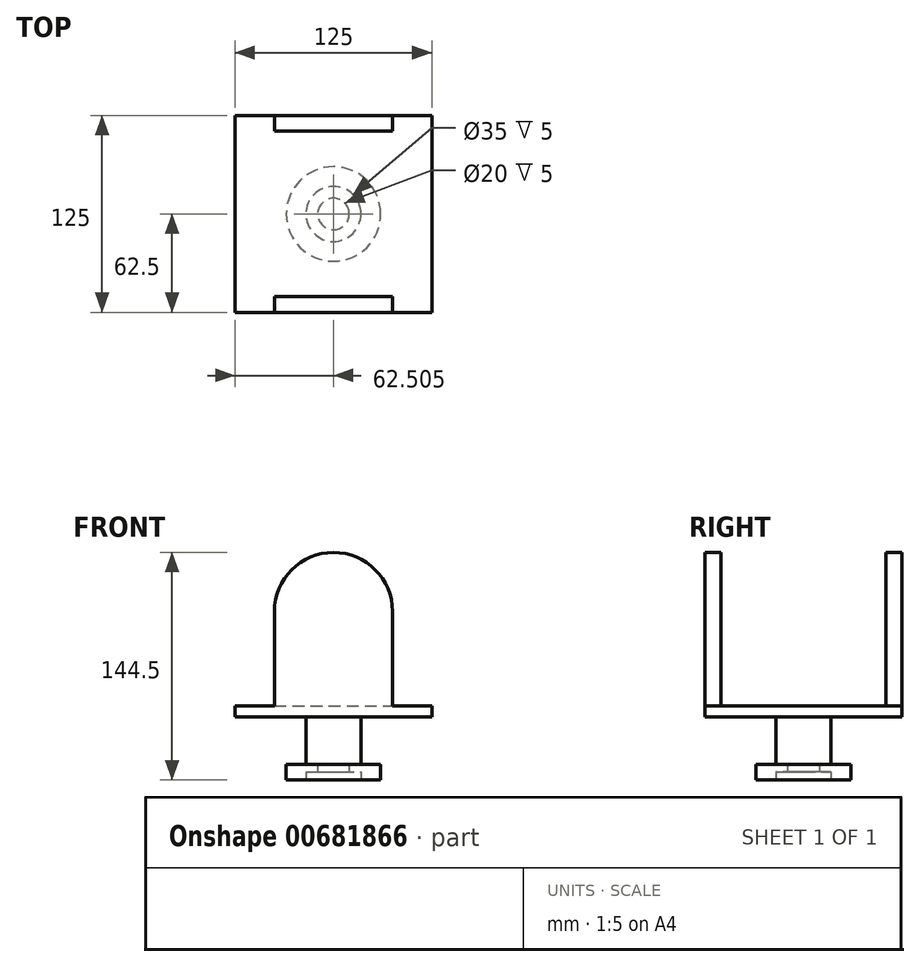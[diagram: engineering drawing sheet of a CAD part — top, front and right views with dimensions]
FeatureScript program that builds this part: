
annotation { "Feature Type Name" : "Feature", "Feature Type Description" : "" }
export const myFeature = defineFeature(function(context is Context, id is Id, definition is map)
    precondition{}
    {
        {
            var Q0;
            Q0=qCreatedBy(makeId("Front.planeOp"),FACE);
            var sketch = newSketch(context, id + "F0", { "sketchPlane" : qUnion([Q0])});
            skLineSegment(sketch, "E0.bottom", {"start": v(-61.18, -9.1) * mm, "end": v(63.82, -9.1) * mm});
            skLineSegment(sketch, "E0.top", {"start": v(-61.18, -16.1) * mm, "end": v(63.82, -16.1) * mm});
            skLineSegment(sketch, "E0.left", {"start": v(-61.18, -9.1) * mm, "end": v(-61.18, -16.1) * mm});
            skLineSegment(sketch, "E0.right", {"start": v(63.82, -9.1) * mm, "end": v(63.82, -16.1) * mm});
            skSolve(sketch);
        }
        {
            var Q0;
            Q0 = qSketchRegion(id + "F0", true);
            extrude(context, id + "F1", {"entities" : qUnion([Q0]), "depth" : 105 * mm, "offsetDistance" : 25 * mm});
        }
        {
            var Q0;
            Q0=makeQuery(id+"F1.opExtrude","CAP_FACE",FACE,{"disambiguationData":[OSD([sQuery(id+"F0.wireOp",EDGE,"E0.bottom"),sQuery(id+"F0.wireOp",EDGE,"E0.top"),sQuery(id+"F0.wireOp",EDGE,"E0.left"),sQuery(id+"F0.wireOp",EDGE,"E0.right")])],"isStart":false});
            var sketch = newSketch(context, id + "F2", { "sketchPlane" : qUnion([Q0])});
            skLineSegment(sketch, "E1.bottom", {"start": v(-61.18, -16.1) * mm, "end": v(63.82, -16.1) * mm});
            skLineSegment(sketch, "E1.top", {"start": v(-61.18, -9.1) * mm, "end": v(63.82, -9.1) * mm});
            skLineSegment(sketch, "E1.left", {"start": v(-61.18, -16.1) * mm, "end": v(-61.18, -9.1) * mm});
            skLineSegment(sketch, "E1.right", {"start": v(63.82, -16.1) * mm, "end": v(63.82, -9.1) * mm});
            skLineSegment(sketch, "E2.bottom", {"start": v(-36.18, -9.1) * mm, "end": v(38.82, -9.1) * mm});
            skLineSegment(sketch, "E2.top", {"start": v(-36.18, 50.9) * mm, "end": v(38.82, 50.9) * mm});
            skLineSegment(sketch, "E2.left", {"start": v(-36.18, -9.1) * mm, "end": v(-36.18, 50.9) * mm});
            skLineSegment(sketch, "E2.right", {"start": v(38.82, -9.1) * mm, "end": v(38.82, 50.9) * mm});
            skArc(sketch, "E3", {"start": v(38.82, 50.9) * mm, "mid": v(1.32, 88.4) * mm, "end": v(-36.18, 50.9) * mm});
            skSolve(sketch);
        }
        {
            var Q0;
            Q0 = qSketchRegion(id + "F2", true);
            extrude(context, id + "F3", {"entities" : qUnion([Q0]), "operationType" : NewBodyOperationType.ADD, "depth" : 10 * mm, "offsetDistance" : 25 * mm});
        }
        {
            var Q0;
            Q0=makeQuery(id+"F1.opExtrude","CAP_FACE",FACE,{"disambiguationData":[OSD([sQuery(id+"F0.wireOp",EDGE,"E0.bottom"),sQuery(id+"F0.wireOp",EDGE,"E0.top"),sQuery(id+"F0.wireOp",EDGE,"E0.left"),sQuery(id+"F0.wireOp",EDGE,"E0.right")])],"isStart":true});
            var sketch = newSketch(context, id + "F4", { "sketchPlane" : qUnion([Q0])});
            skLineSegment(sketch, "E4.bottom", {"start": v(-63.82, -16.1) * mm, "end": v(61.18, -16.1) * mm});
            skLineSegment(sketch, "E4.top", {"start": v(-63.82, -9.1) * mm, "end": v(61.18, -9.1) * mm});
            skLineSegment(sketch, "E4.left", {"start": v(-63.82, -16.1) * mm, "end": v(-63.82, -9.1) * mm});
            skLineSegment(sketch, "E4.right", {"start": v(61.18, -16.1) * mm, "end": v(61.18, -9.1) * mm});
            skLineSegment(sketch, "E5.bottom", {"start": v(-38.82, -9.1) * mm, "end": v(36.18, -9.1) * mm});
            skLineSegment(sketch, "E5.top", {"start": v(-38.82, 50.9) * mm, "end": v(36.18, 50.9) * mm});
            skLineSegment(sketch, "E5.left", {"start": v(-38.82, -9.1) * mm, "end": v(-38.82, 50.9) * mm});
            skLineSegment(sketch, "E5.right", {"start": v(36.18, -9.1) * mm, "end": v(36.18, 50.9) * mm});
            skArc(sketch, "E6", {"start": v(36.18, 50.9) * mm, "mid": v(-1.32, 88.4) * mm, "end": v(-38.82, 50.9) * mm});
            skSolve(sketch);
        }
        {
            var Q0;
            Q0 = qSketchRegion(id + "F4", true);
            extrude(context, id + "F5", {"entities" : qUnion([Q0]), "operationType" : NewBodyOperationType.ADD, "depth" : 10 * mm, "offsetDistance" : 25 * mm});
        }
        {
            var Q0;
            Q0=makeQuery(id+"F5.boolean.opBoolean","MERGE",FACE,{"derivedFrom":[makeQuery(id+"F3.boolean.opBoolean","MERGE",FACE,{"derivedFrom":[makeQuery(id+"F1.opExtrude","SWEPT_FACE",FACE,{"disambiguationData":[OSD([sQuery(id+"F0.wireOp",EDGE,"E0.top")])]}),makeQuery(id+"F3.opExtrude","SWEPT_FACE",FACE,{"disambiguationData":[OSD([sQuery(id+"F2.wireOp",EDGE,"E1.bottom")])]})]}),makeQuery(id+"F5.opExtrude","SWEPT_FACE",FACE,{"disambiguationData":[OSD([sQuery(id+"F4.wireOp",EDGE,"E4.bottom")])]})]});
            var sketch = newSketch(context, id + "F6", { "sketchPlane" : qUnion([Q0])});
            skLineSegment(sketch, "E7", {"start": v(1.32, 115) * mm, "end": v(1.32, -10) * mm});
            skLineSegment(sketch, "E8", {"start": v(-61.18, 52.5) * mm, "end": v(63.82, 52.5) * mm});
            skCircle(sketch, "E9", {"center": v(1.32, 52.5) * mm, "radius": 17.5 * mm});
            skSolve(sketch);
        }
        {
            var Q0;
            Q0 = qSketchRegion(id + "F6", true);
            extrude(context, id + "F7", {"entities" : qUnion([Q0]), "operationType" : NewBodyOperationType.ADD, "depth" : 30 * mm, "offsetDistance" : 25 * mm});
        }
        {
            var Q0;
            Q0=makeQuery(id+"F7.opExtrude","CAP_FACE",FACE,{"disambiguationData":[OSD([sQuery(id+"F6.wireOp",EDGE,"E9")])],"isStart":false});
            var sketch = newSketch(context, id + "F8", { "sketchPlane" : qUnion([Q0])});
            skCircle(sketch, "E10", {"center": v(1.32, 52.5) * mm, "radius": 30 * mm});
            skSolve(sketch);
        }
        {
            var Q0;
            Q0 = qSketchRegion(id + "F8", true);
            extrude(context, id + "F9", {"entities" : qUnion([Q0]), "operationType" : NewBodyOperationType.ADD, "depth" : 10 * mm, "offsetDistance" : 25 * mm});
        }
        {
            var Q0;
            Q0=makeQuery(id+"F9.opExtrude","CAP_FACE",FACE,{"disambiguationData":[OSD([sQuery(id+"F8.wireOp",EDGE,"E10")])],"isStart":false});
            var sketch = newSketch(context, id + "F10", { "sketchPlane" : qUnion([Q0])});
            skCircle(sketch, "E11", {"center": v(1.32, 52.5) * mm, "radius": 17.5 * mm});
            skSolve(sketch);
        }
        {
            var Q0;
            Q0 = qSketchRegion(id + "F10", true);
            extrude(context, id + "F11", {"entities" : qUnion([Q0]), "operationType" : NewBodyOperationType.REMOVE, "oppositeDirection" : true, "depth" : 5 * mm, "offsetDistance" : 25 * mm});
        }
        {
            var Q0;
            Q0=makeQuery(id+"F11.boolean.opBoolean","COPY",FACE,{"derivedFrom":makeQuery(id+"F11.opExtrude","CAP_FACE",FACE,{"disambiguationData":[OSD([sQuery(id+"F10.wireOp",EDGE,"E11")])],"isStart":false})});
            var sketch = newSketch(context, id + "F12", { "sketchPlane" : qUnion([Q0])});
            skCircle(sketch, "E12", {"center": v(1.32, 52.5) * mm, "radius": 10 * mm});
            skSolve(sketch);
        }
        {
            var Q0;
            Q0 = qSketchRegion(id + "F12", true);
            extrude(context, id + "F13", {"entities" : qUnion([Q0]), "operationType" : NewBodyOperationType.REMOVE, "oppositeDirection" : true, "depth" : 5 * mm, "offsetDistance" : 25 * mm});
        }
    });
